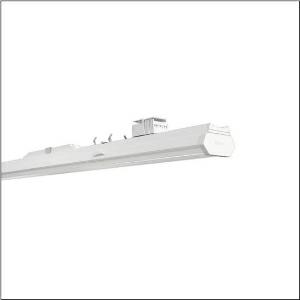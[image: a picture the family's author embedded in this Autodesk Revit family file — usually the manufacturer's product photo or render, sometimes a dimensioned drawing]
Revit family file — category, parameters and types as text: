
# Revit family: licross_11_protected_mo_51td1bdn68xg
name_source: partatom
category: Lighting Fixtures
units: mm (PartAtom-declared; Revit-internal decimal feet)

## family parameters
Cut with Voids When Loaded = No
Host = Face
Light Source = No
Part Type = Normal
Room Calculation Point = No
Round Connector Dimension = Use Diameter
Shared = No

## types (1)
- --- (1 x LED, 8310 lm, 51.3 W, 6500K)
    Apparent Load = 51 VA
    CIE Flux Codes = 54 82 95 97 100
    Color Rendering = 80
    Color Temperature = 6500K
    Default Elevation = 1800 mm
    Description = Licross 11 Protected MO, luminaire insert, of sheet steel, galvanised, coil coated, white, length: 1.500mm, width: 90mm, height: 101mm, LED rated luminous flux: 8.310lm, light colour: 865, SDCM (Standard Deviation of Colour Matching)MacAdam ≤ 2 SDCM (initial), control gear: DALI 2, with plug, 5-pole, with phase selection, mains connection: 220..240V, AC, 50/60Hz, rated input power: 51W, internal wiring halogen-free, primary optical cover: cover, of PMMA, light emission: direct distribution, primary light characteristic: symmetric, protection rating (complete): IP54, insulation class (complete): insulation class I (protective earthing), certification: CE, ENEC, VDE, UKCA, protection symbol: D if used in an environment with non-conductive dust loads with corresponding accessories, impact resistance: IK06, permissible ambient temperature for indoor applications: -25..+35°C, corresponds to IFS (International Featured Standards) requirements for safety and quality in the food industry, reducing of maximum allowable ambient temperature of 5°C with ceiling mounting, LABS conformity tested according to VDMA 24364:2018-05, The light source and the operating device comply with the requirements of the Ecodesign Regulation (EU) 2019/2020 and are replaceable in accordance with this regulation, packaging unit: 1 piece
    Height = 92 mm
    Lamp = 1 x LED
    Lamp Light Flux = 8310 lm
    Lamp Power = 51.3 W
    Lamp count = 1
    Length = 1500 mm
    Luminous efficacy = 162 lm/W
    Manufacturer = Siteco
    ModVariant = No
    Model = 51TD1BDN68XG
    Mounting Place = Ceiling
    Mounting Type = Pendant
    Number of Poles = 1
    OnlyDefault = Yes
    Power Factor = 1
    Product Name = Licross 11 Protected MO
    Product group = luminaire insert | ceiling pendant
    ProductGroupID = 901
    Protection Class = Protection class I
    Protection Degree = IP 54
    RLX_Detail_Level = 1
    RLX_Emergency_Light_Flux = 0 lm
    RLX_Emergency_Type = 0
    RLX_Emergency_Type_DB = No
    RlxData = <blob elided: 24677 chars, md5=caa964a2>
    Socket = socket
    Standby Power = 0 W
    System Light Flux = 8310 lm
    System Power = 51 W
    Type Comments = factory setting: luminous flux: 100 % | dim-lin: 254 | 341 mA
    Type Image = l_1256145.jpg
    URL = http://relux.com
    VarID = @adj_056161
    Voltage = 0 V
    Weight = 0.00 kg
    Width = 88 mm

## geometry (parser evidence)
native form markers: Blend x4, Sweep x9
no freeform markers — native parametric forms only
